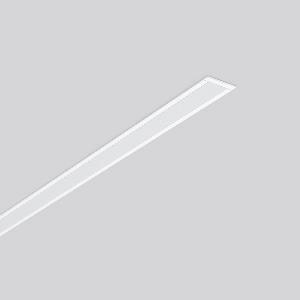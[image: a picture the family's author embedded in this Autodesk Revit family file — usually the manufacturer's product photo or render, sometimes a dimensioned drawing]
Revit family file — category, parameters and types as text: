
# Revit family: less_is_more_27_312176_002_76_0731
name_source: partatom
category: Lighting Fixtures
units: mm (PartAtom-declared; Revit-internal decimal feet)

## family parameters
Cut with Voids When Loaded = No
Host = Face
Light Source = No
Part Type = Normal
Room Calculation Point = No
Round Connector Dimension = Use Diameter
Shared = No

## types (1)
- LESS IS MORE 27 (1 x LED Modul 830, 1950 lm, 3000)
    Apparent Load = 29 VA
    CIE Flux Codes = 48 79 96 100 100
    Color Rendering = 80
    Color Temperature = 3000
    Default Elevation = 1800 mm
    Description = Series: LESS IS MORE 27
Recessed ceiling and wall luminaire with slim design. Housing: extruded aluminium profile, powder-coated. End cap aluminium powder-coated. Diffuser made of non-yellowing plastic (PMMA), opal. Suitable for Recessed ceiling mounting, wall (recessed). External driver with connecting cable. 
Colour: traffic white, matt (RAL 9016)
Length: 1014 mm
Width: 38 mm
Height: 2 mm
Cut-out length: 1006 mm
Cut-out width: 30 mm
Recess height: 45-60 mm
Luminaire: recess height: 37 mm
Lamp: LED
Socket: without socket
Colour temperature: 3000K
Colour rendering index (CRI): 82
System power: 29 W
Rated luminous flux: 1950 lm
Luminous efficiency: 67 lm/W
Control gear: Voltage converter, DALI dim.
Protection class: II
Type of protection: IP 20
    Height = 0 mm  [stored 0 ft]
    Lamp = 1 x LED Modul 830
    Lamp Light Flux = 1950 lm
    Lamp count = 1
    Length = 1014 mm
    Lifetime = 50000 h
    Luminous efficacy = 67 lm/W
    Manufacturer = RZB
    ModVariant = No
    Model = 312176.002.76
    Mounting Place = Ceiling, Wall
    Mounting Type = Recessed
    Number of Poles = 1
    OnlyDefault = Yes
    Power Factor = 1
    Product Name = LESS IS MORE 27
    Product group = Recessed LED linear luminaires
    ProductGroupID = 407
    Protection Class = Protection class II
    Protection Degree = IP 20
    RLX_Detail_Level = 1
    RLX_Emergency_Light_Flux = 0 lm
    RLX_Emergency_Type = 0
    RLX_Emergency_Type_DB = No
    RlxData = <blob elided: 21589 chars, md5=f9b10500>
    Socket = socket
    Standby Power = 0 W
    System Light Flux = 1950 lm
    System Power = 29 W
    Type Comments = Product without accessories
    Type Image = 312176.002.jpg
    URL = http://relux.com
    VarID = ---
    Voltage = 230 V
    Voltage Range = 220-240 V
    Weight = 0.00 kg
    Width = 38 mm

note: [stored X ft] marks values corroborated as IEEE doubles in the binary element streams (Revit-internal decimal feet)

## geometry (parser evidence)
native form markers: Blend x4, Sweep x11
no freeform markers — native parametric forms only
